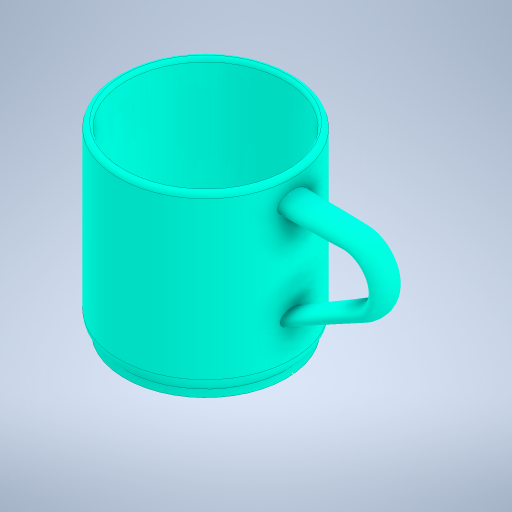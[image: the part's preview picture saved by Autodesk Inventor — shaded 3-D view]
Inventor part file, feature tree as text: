
AUTODESK INVENTOR PART (.ipt)
format: ipt  version: 2023 (Build 270158000, 158)  size: 365,568 bytes
history: native  units: mm
features: sketch x7, other x3, plane x2, revolve x1, shell x1, loft x1, fillet x1, extrude x1
ambient origin geometry x8: Origin, YZ Plane, XZ Plane, XY Plane, X Axis, Y Axis, Z Axis, Center Point
bodies: Body1 (feature_tree)
feature tree (17):
  other  "Sección transversal1"
  other  "Sección transversal2"
  other  "Sólido1"
  revolve  "Revolución1"  [1 undecoded]
  shell  "Vaciado1"  Thickness=65.0mm
  sketch  "Boceto2"  dims[d3=32.5mm d4=90.0deg d5=3.0mm]
  sketch  "Boceto3"  dims[d6=0.5mm d7=2.0mm d8=0.0mm d9=20.0mm d10=0.5mm d11=2.0mm d12=0.0mm d13=20.0mm d14=25.0mm]
  plane  "Plano de trabajo1"
  sketch  "Boceto4"  dims[d15=10.0mm]
  plane  "Plano de trabajo2"
  sketch  "Boceto5"  dims[d16=12.0mm]
  loft  "Solevación1"
  fillet  "Empalme1"  Radius=3.0mm
  extrude  "Extrusión1"  Depth=2.0mm
  sketch  "Boceto1"  dims[d0=70.0mm d1=35.0mm d2=65.0mm]
  sketch  "Boceto6"  dims[d17=15.0mm]
  sketch  "Boceto7"  dims[d18=4.0mm d19=6.0mm d20=3.0mm d21=5.0mm d22=0.0mm d23=90.0deg d24=0.0mm d25=90.0deg d26=0.0mm d27=90.0deg d28=2.0mm d29=65.0mm d30=62.0mm d31=3.0mm d32=0.0mm d33=0.5mm d34=0.872665mm]
note: 1 required parameter value undecoded (feature->parameter linkage not recoverable at this tier; creation-order binding heuristic only, values carry confidence <= 0.55)
